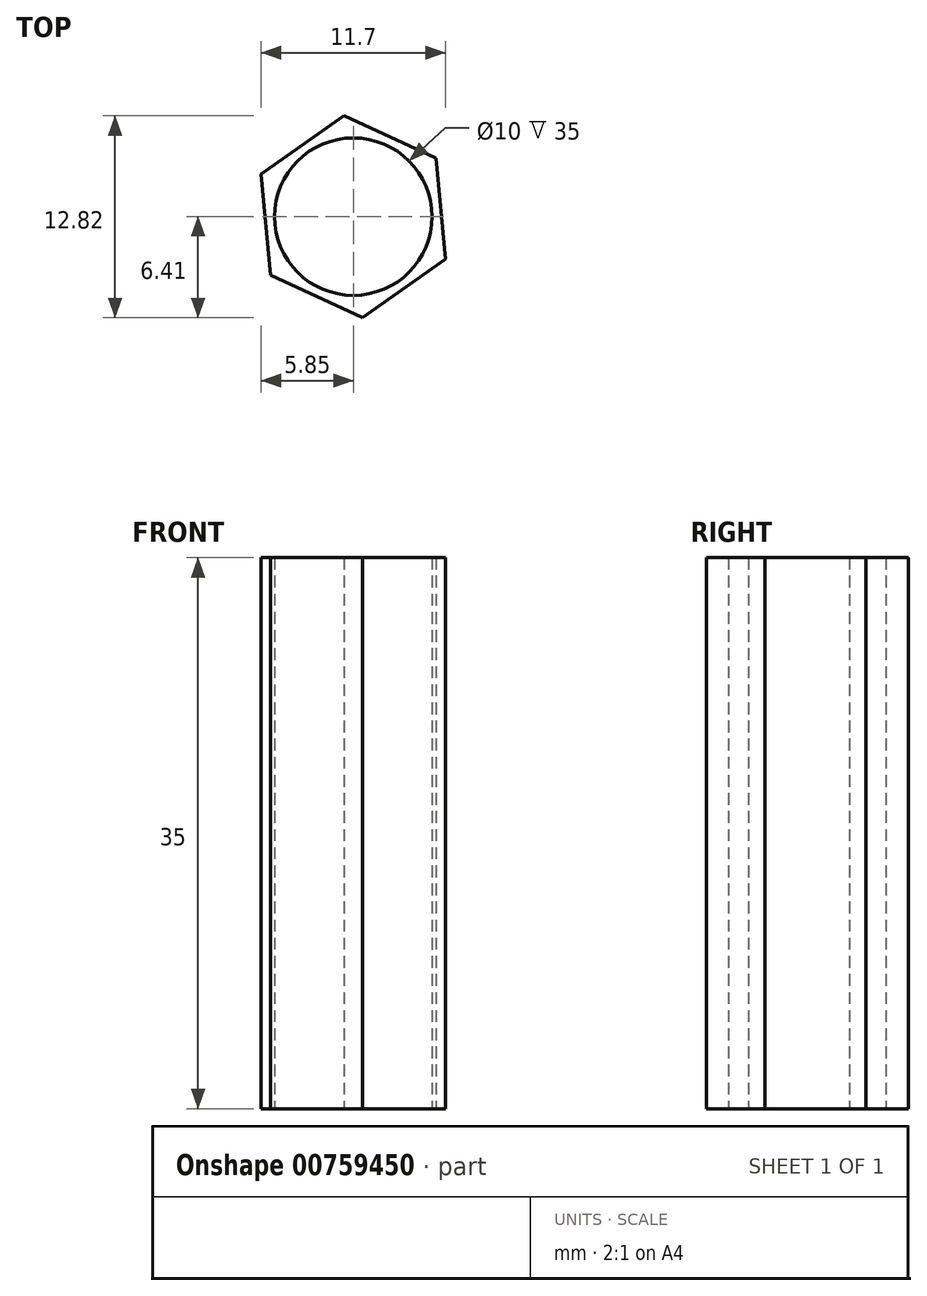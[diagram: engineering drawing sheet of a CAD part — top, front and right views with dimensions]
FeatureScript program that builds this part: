
annotation { "Feature Type Name" : "Feature", "Feature Type Description" : "" }
export const myFeature = defineFeature(function(context is Context, id is Id, definition is map)
    precondition{}
    {
        {
            var Q0;
            Q0=qCreatedBy(makeId("Top.planeOp"),FACE);
            var sketch = newSketch(context, id + "F0", { "sketchPlane" : qUnion([Q0])});
            skCircle(sketch, "E0", {"center": v(0, 0) * mm, "radius": 5 * mm});
            skCircle(sketch, "E1.cCircle", {"center": v(0, 0) * mm, "radius": 5.58 * mm, "construction": true});
            skLineSegment(sketch, "E1.0", {"start": v(5.85, -2.7) * mm, "end": v(0.6, -6.41) * mm});
            skLineSegment(sketch, "E1.1", {"start": v(0.6, -6.41) * mm, "end": v(-5.26, -3.72) * mm});
            skLineSegment(sketch, "E1.2", {"start": v(-5.26, -3.72) * mm, "end": v(-5.85, 2.7) * mm});
            skLineSegment(sketch, "E1.3", {"start": v(-5.85, 2.7) * mm, "end": v(-0.6, 6.41) * mm});
            skLineSegment(sketch, "E1.4", {"start": v(-0.6, 6.41) * mm, "end": v(5.26, 3.72) * mm});
            skLineSegment(sketch, "E1.5", {"start": v(5.26, 3.72) * mm, "end": v(5.85, -2.7) * mm});
            skPoint(sketch, "E1.0.midPoint", {"position": v(3.22, -4.55) * mm});
            skSolve(sketch);
        }
        {
            var Q0;
            Q0=makeQuery(id+"F0.imprint","IMPRINT",FACE,{"disambiguationData":[TD([[makeQuery(id+"F0.imprint","IMPRINT",EDGE,{"derivedFrom":sQuery(id+"F0.wireOp",EDGE,"E0")}),-1.0]])]});
            extrude(context, id + "F1", {"entities" : qUnion([Q0]), "depth" : 35 * mm, "offsetDistance" : 25 * mm});
        }
    });
